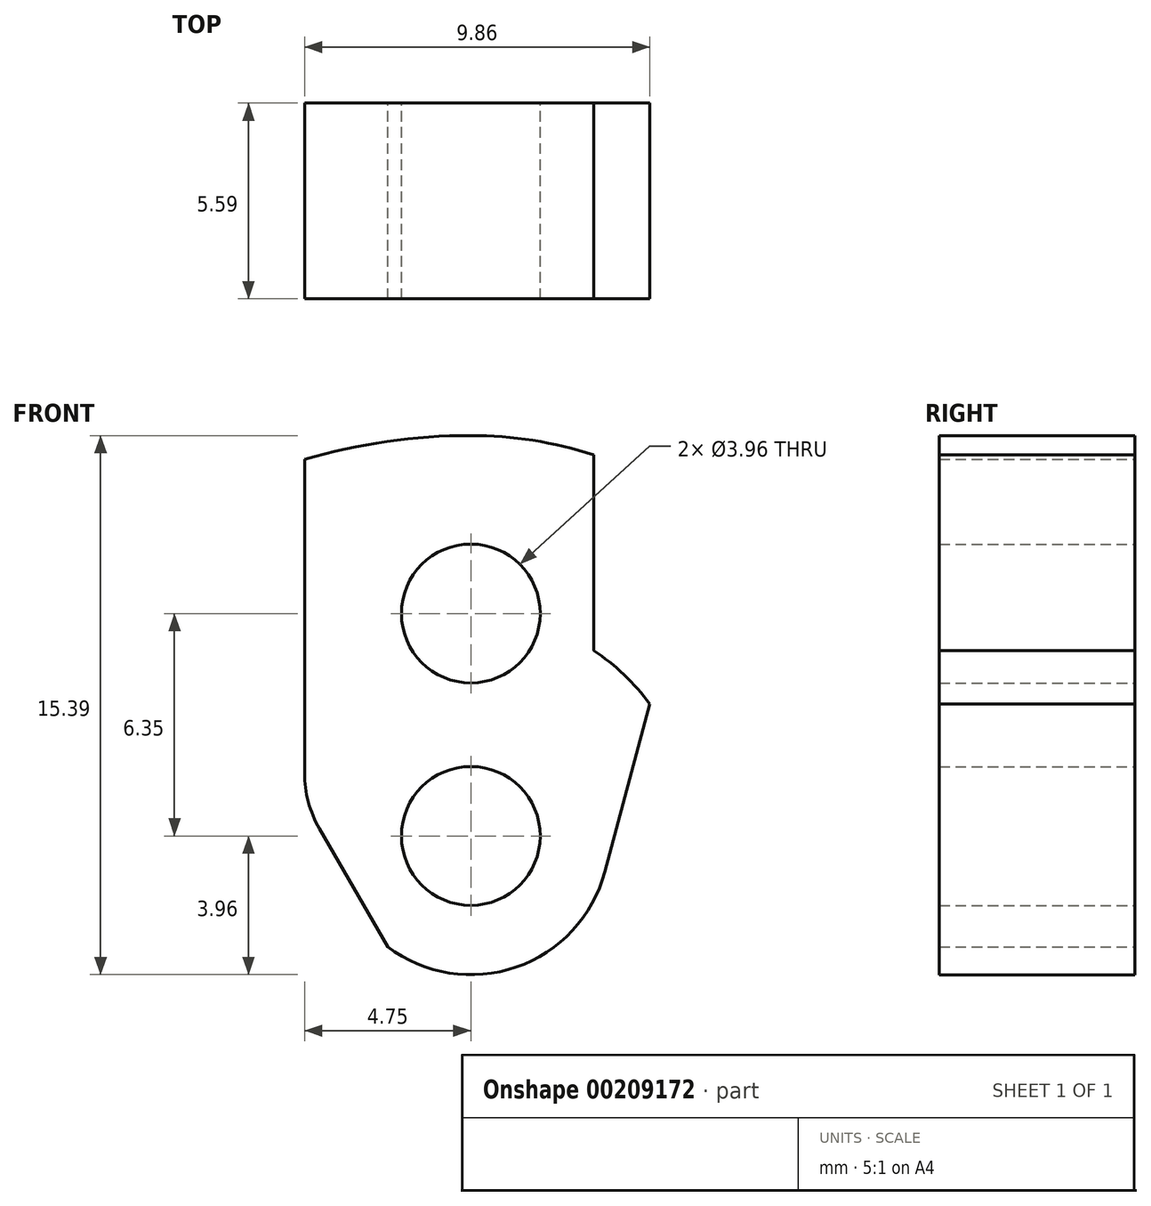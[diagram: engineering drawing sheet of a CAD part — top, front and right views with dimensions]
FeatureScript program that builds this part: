
annotation { "Feature Type Name" : "Feature", "Feature Type Description" : "" }
export const myFeature = defineFeature(function(context is Context, id is Id, definition is map)
    precondition{}
    {
        {
            var Q0;
            Q0=qCreatedBy(makeId("Front.planeOp"),FACE);
            var sketch = newSketch(context, id + "F0", { "sketchPlane" : qUnion([Q0])});
            skCircle(sketch, "E0", {"center": v(0, 0) * mm, "radius": 1.98 * mm});
            skCircle(sketch, "E1", {"center": v(0, 6.35) * mm, "radius": 1.98 * mm});
            skArc(sketch, "E2", {"start": v(-2.38, -3.17) * mm, "mid": v(1.3, -3.74) * mm, "end": v(3.83, -1.03) * mm});
            skLineSegment(sketch, "E3", {"start": v(-4.75, 4.52) * mm, "end": v(-4.75, 10.75) * mm});
            skLineSegment(sketch, "E4", {"start": v(-4.75, 4.52) * mm, "end": v(-4.75, 1.8) * mm});
            skLineSegment(sketch, "E5", {"start": v(-2.38, -3.17) * mm, "end": v(-4.32, 0.2) * mm});
            skPoint(sketch, "E6.visualSharp", {"position": v(-4.75, 0.94) * mm});
            skArc(sketch, "E6.filletArc", {"start": v(-4.75, 1.8) * mm, "mid": v(-4.64, 0.97) * mm, "end": v(-4.32, 0.2) * mm});
            skLineSegment(sketch, "E7", {"start": v(3.83, -1.03) * mm, "end": v(5.11, 3.77) * mm});
            skArc(sketch, "E8", {"start": v(5.11, 3.77) * mm, "mid": v(4.38, 4.6) * mm, "end": v(3.5, 5.3) * mm});
            skLineSegment(sketch, "E9", {"start": v(3.5, 6.35) * mm, "end": v(3.5, 10.75) * mm});
            skLineSegment(sketch, "E10", {"start": v(3.5, 6.35) * mm, "end": v(3.5, 5.3) * mm});
            skArc(sketch, "E11", {"start": v(3.5, 10.88) * mm, "mid": v(1.77, 11.3) * mm, "end": v(0, 11.43) * mm});
            skLineSegment(sketch, "E12", {"start": v(3.5, 10.75) * mm, "end": v(3.5, 10.88) * mm});
            skArc(sketch, "E13", {"start": v(0, 11.43) * mm, "mid": v(-2.4, 11.26) * mm, "end": v(-4.75, 10.75) * mm});
            skSolve(sketch);
        }
        {
            var Q0;
            Q0 = qSketchRegion(id + "F0", true);
            extrude(context, id + "F1", {"entities" : qUnion([Q0]), "depth" : 5.6 * mm});
        }
    });
